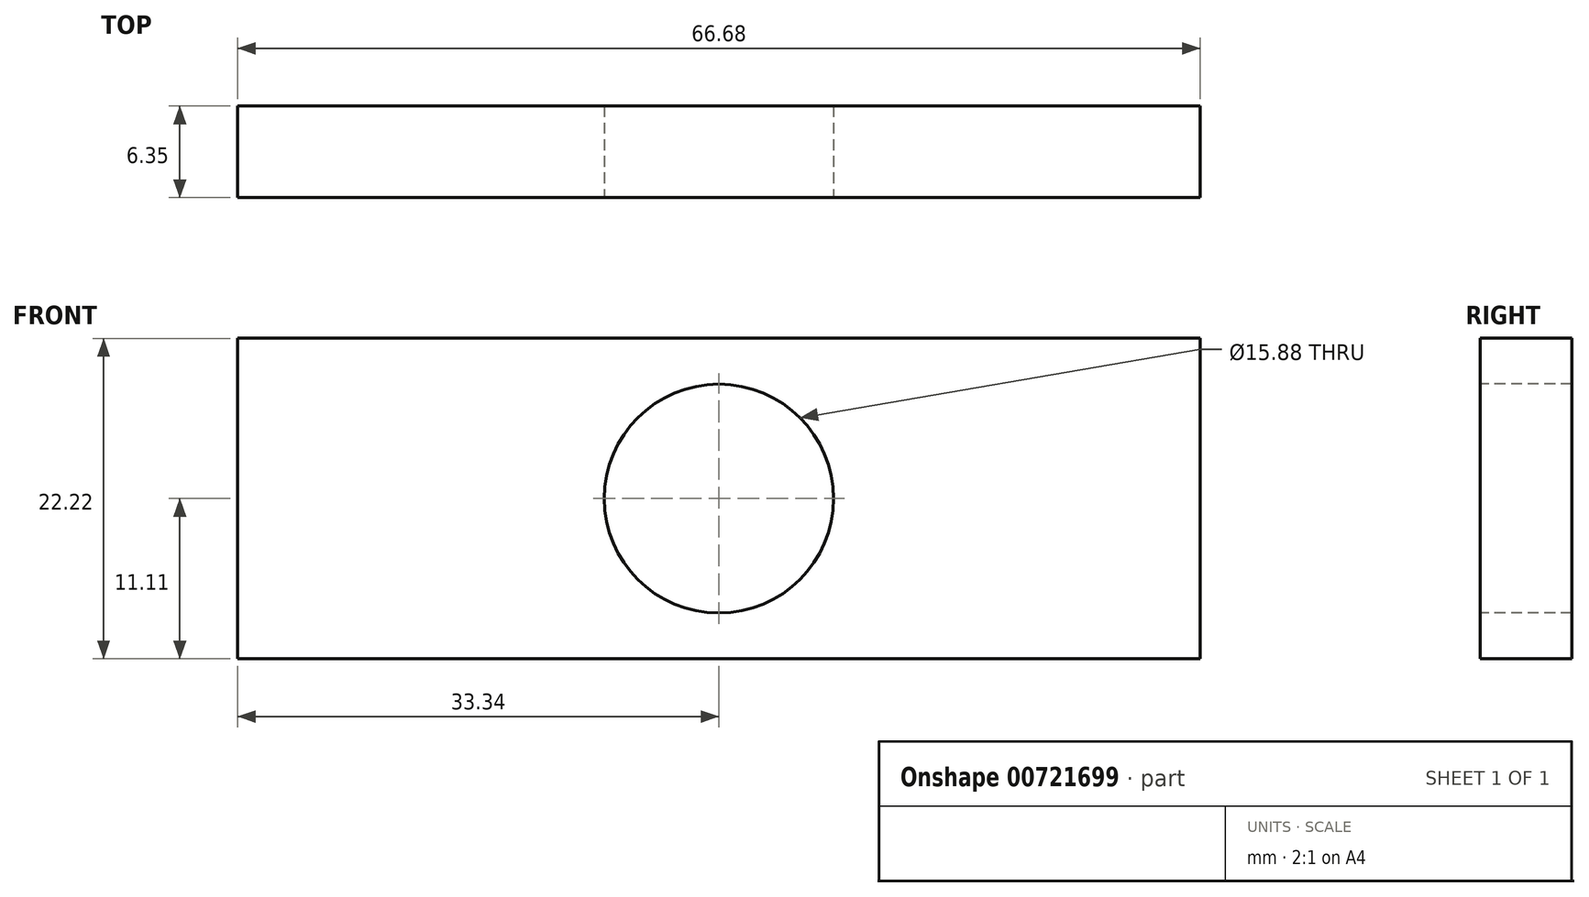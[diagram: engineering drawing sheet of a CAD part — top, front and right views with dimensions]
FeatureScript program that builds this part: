
annotation { "Feature Type Name" : "Feature", "Feature Type Description" : "" }
export const myFeature = defineFeature(function(context is Context, id is Id, definition is map)
    precondition{}
    {
        {
            var Q0;
            Q0=qCreatedBy(makeId("Front.planeOp"),FACE);
            var sketch = newSketch(context, id + "F0", { "sketchPlane" : qUnion([Q0])});
            skLineSegment(sketch, "E0", {"start": v(0, 11.11) * mm, "end": v(0, -46.32) * mm, "construction": true});
            skLineSegment(sketch, "E1", {"start": v(-49.04, 0) * mm, "end": v(58.02, 0) * mm, "construction": true});
            skLineSegment(sketch, "E2", {"start": v(-33.34, 11.11) * mm, "end": v(33.34, 11.11) * mm});
            skLineSegment(sketch, "E3.MirrorCS", {"start": v(-33.34, -11.11) * mm, "end": v(33.34, -11.11) * mm});
            skLineSegment(sketch, "E4", {"start": v(-33.34, 11.11) * mm, "end": v(-33.34, -11.11) * mm});
            skLineSegment(sketch, "E5.MirrorCS", {"start": v(33.34, 11.11) * mm, "end": v(33.34, -11.11) * mm});
            skCircle(sketch, "E6", {"center": v(0, 0) * mm, "radius": 7.94 * mm});
            skSolve(sketch);
        }
        {
            var Q0;
            Q0 = qSketchRegion(id + "F0", true);
            extrude(context, id + "F1", {"entities" : qUnion([Q0]), "oppositeDirection" : true, "depth" : 6.35 * mm, "offsetDistance" : 25.4 * mm});
        }
    });
